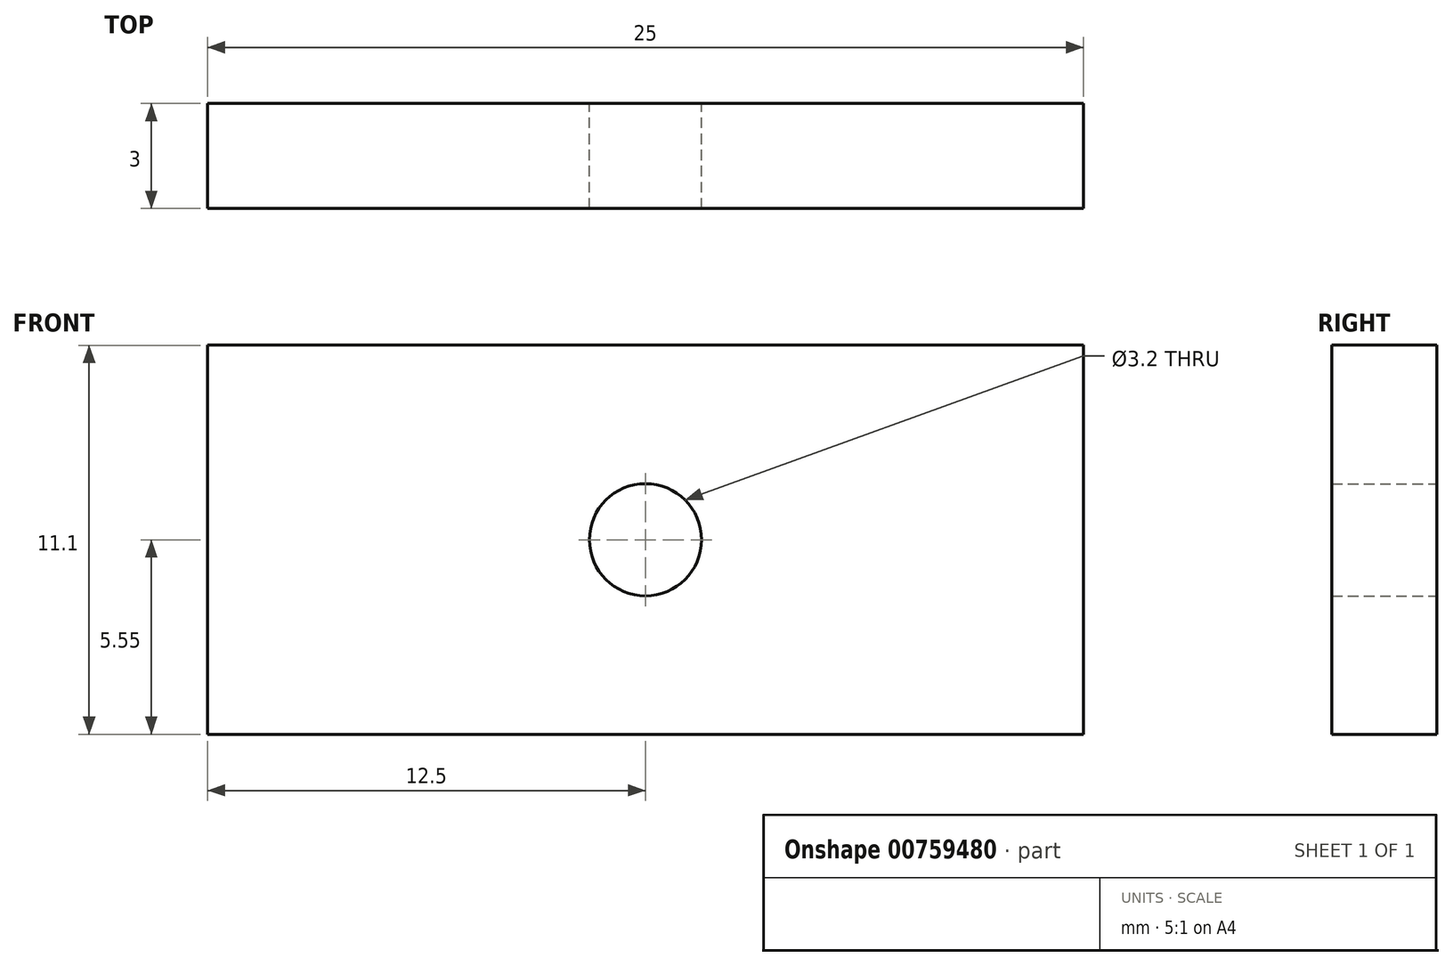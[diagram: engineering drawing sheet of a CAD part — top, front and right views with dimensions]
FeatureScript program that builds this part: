
annotation { "Feature Type Name" : "Feature", "Feature Type Description" : "" }
export const myFeature = defineFeature(function(context is Context, id is Id, definition is map)
    precondition{}
    {
        {
            var Q0;
            Q0=qCreatedBy(makeId("Front.planeOp"),FACE);
            var sketch = newSketch(context, id + "F0", { "sketchPlane" : qUnion([Q0])});
            skLineSegment(sketch, "E0.bottom", {"start": v(-12.5, 5.56) * mm, "end": v(12.5, 5.56) * mm});
            skLineSegment(sketch, "E0.top", {"start": v(-12.5, -5.55) * mm, "end": v(12.5, -5.55) * mm});
            skLineSegment(sketch, "E0.left", {"start": v(-12.5, 5.56) * mm, "end": v(-12.5, -5.56) * mm});
            skLineSegment(sketch, "E0.right", {"start": v(12.5, 5.56) * mm, "end": v(12.5, -5.56) * mm});
            skPoint(sketch, "E0.middle", {"position": v(0, 0) * mm});
            skCircle(sketch, "E1", {"center": v(0, 0) * mm, "radius": 1.6 * mm});
            skSolve(sketch);
        }
        {
            var Q0;
            Q0=makeQuery(id+"F0.imprint","IMPRINT",FACE,{"disambiguationData":[TD([[makeQuery(id+"F0.imprint","IMPRINT",EDGE,{"derivedFrom":sQuery(id+"F0.wireOp",EDGE,"E0.bottom")}),-1.0]])]});
            extrude(context, id + "F1", {"entities" : qUnion([Q0]), "depth" : 3 * mm, "offsetDistance" : 25 * mm});
        }
    });
